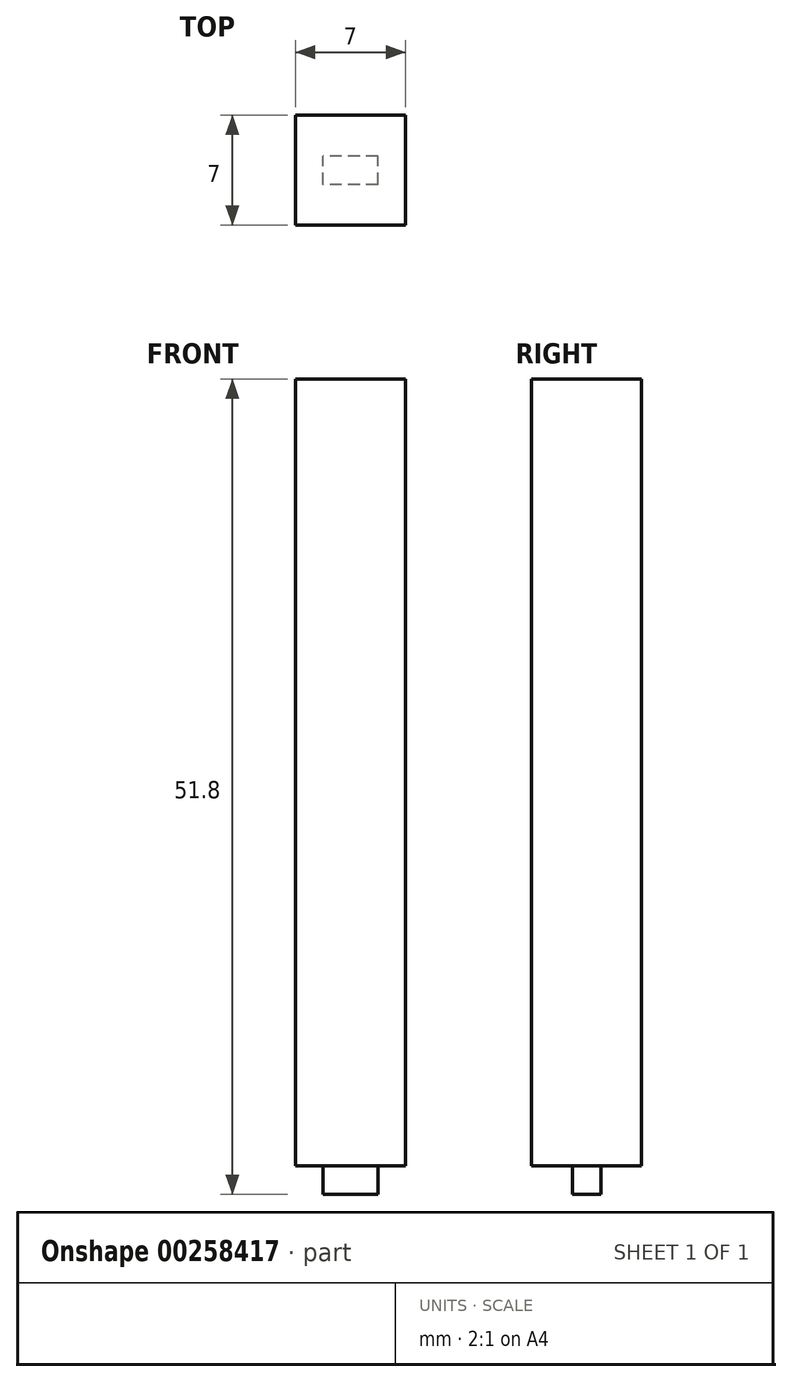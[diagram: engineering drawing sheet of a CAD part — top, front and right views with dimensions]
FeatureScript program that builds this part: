
annotation { "Feature Type Name" : "Feature", "Feature Type Description" : "" }
export const myFeature = defineFeature(function(context is Context, id is Id, definition is map)
    precondition{}
    {
        {
            var Q0;
            Q0=qCreatedBy(makeId("Front.planeOp"),FACE);
            var sketch = newSketch(context, id + "F0", { "sketchPlane" : qUnion([Q0])});
            skLineSegment(sketch, "E0.bottom", {"start": v(1.75, -26.35) * mm, "end": v(-1.75, -26.35) * mm});
            skLineSegment(sketch, "E0.left", {"start": v(1.75, -26.35) * mm, "end": v(1.75, -24.55) * mm});
            skLineSegment(sketch, "E0.right", {"start": v(-1.75, -26.35) * mm, "end": v(-1.75, -24.55) * mm});
            skPoint(sketch, "E0.middle", {"position": v(0, -25.45) * mm});
            skPoint(sketch, "E1.orphan", {"position": v(3.26, -25.45) * mm});
            skPoint(sketch, "E2.orphan", {"position": v(-3.26, -25.45) * mm});
            skLineSegment(sketch, "E3", {"start": v(-1.75, -24.55) * mm, "end": v(1.75, -24.55) * mm});
            skSolve(sketch);
        }
        {
            var Q0;
            Q0=makeQuery(id+"F0.imprint","IMPRINT",FACE,{"disambiguationData":[TD([[makeQuery(id+"F0.imprint","IMPRINT",EDGE,{"derivedFrom":sQuery(id+"F0.wireOp",EDGE,"1IHOuRVL-ZR1P-SJF7-VTVK-bAyodZimcCda.top")}),1.0]])]});
            var Q1;
            Q1=makeQuery(id+"F0.imprint","IMPRINT",FACE,{"disambiguationData":[TD([[makeQuery(id+"F0.imprint","IMPRINT",EDGE,{"derivedFrom":sQuery(id+"F0.wireOp",EDGE,"E0.bottom")}),-1.0]])]});
            extrude(context, id + "F1", {"entities" : qUnion([Q0, Q1]), "depth" : 1.8 * mm});
        }
        {
            var Q0;
            Q0=makeQuery(id+"F1.opExtrude","SWEPT_FACE",FACE,{"disambiguationData":[OSD([sQuery(id+"F0.wireOp",EDGE,"E3")])]});
            var sketch = newSketch(context, id + "F2", { "sketchPlane" : qUnion([Q0])});
            skLineSegment(sketch, "E4", {"start": v(0, 0) * mm, "end": v(0, -1.8) * mm, "construction": true});
            skLineSegment(sketch, "E5", {"start": v(-1.75, -0.9) * mm, "end": v(1.75, -0.9) * mm, "construction": true});
            skLineSegment(sketch, "E6.bottom", {"start": v(3.5, -4.4) * mm, "end": v(-3.5, -4.4) * mm});
            skLineSegment(sketch, "E6.top", {"start": v(3.5, 2.6) * mm, "end": v(-3.5, 2.6) * mm});
            skLineSegment(sketch, "E6.left", {"start": v(3.5, -4.4) * mm, "end": v(3.5, 2.6) * mm});
            skLineSegment(sketch, "E6.right", {"start": v(-3.5, -4.4) * mm, "end": v(-3.5, 2.6) * mm});
            skPoint(sketch, "E6.middle", {"position": v(0, -0.9) * mm});
            skSolve(sketch);
        }
        {
            var Q0;
            {var subQ0=sQuery(id+"F0.wireOp",EDGE,"E3");Q0=makeQuery(id+"F2.imprint","IMPRINT",FACE,{"disambiguationData":[TD([[makeQuery(id+"F2.imprint","IMPRINT",EDGE,{"derivedFrom":makeQuery(id+"F1.opExtrude","CAP_EDGE",EDGE,{"disambiguationData":[OSD([subQ0])],"isStart":true})}),-1.0]])]});}
            var Q1;
            Q1=makeQuery(id+"F2.imprint","IMPRINT",FACE,{"disambiguationData":[TD([[makeQuery(id+"F2.imprint","IMPRINT",EDGE,{"derivedFrom":sQuery(id+"F2.wireOp",EDGE,"E6.bottom")}),-1.0]])]});
            extrude(context, id + "F3", {"entities" : qUnion([Q0, Q1]), "operationType" : NewBodyOperationType.ADD, "depth" : 50 * mm});
        }
    });
